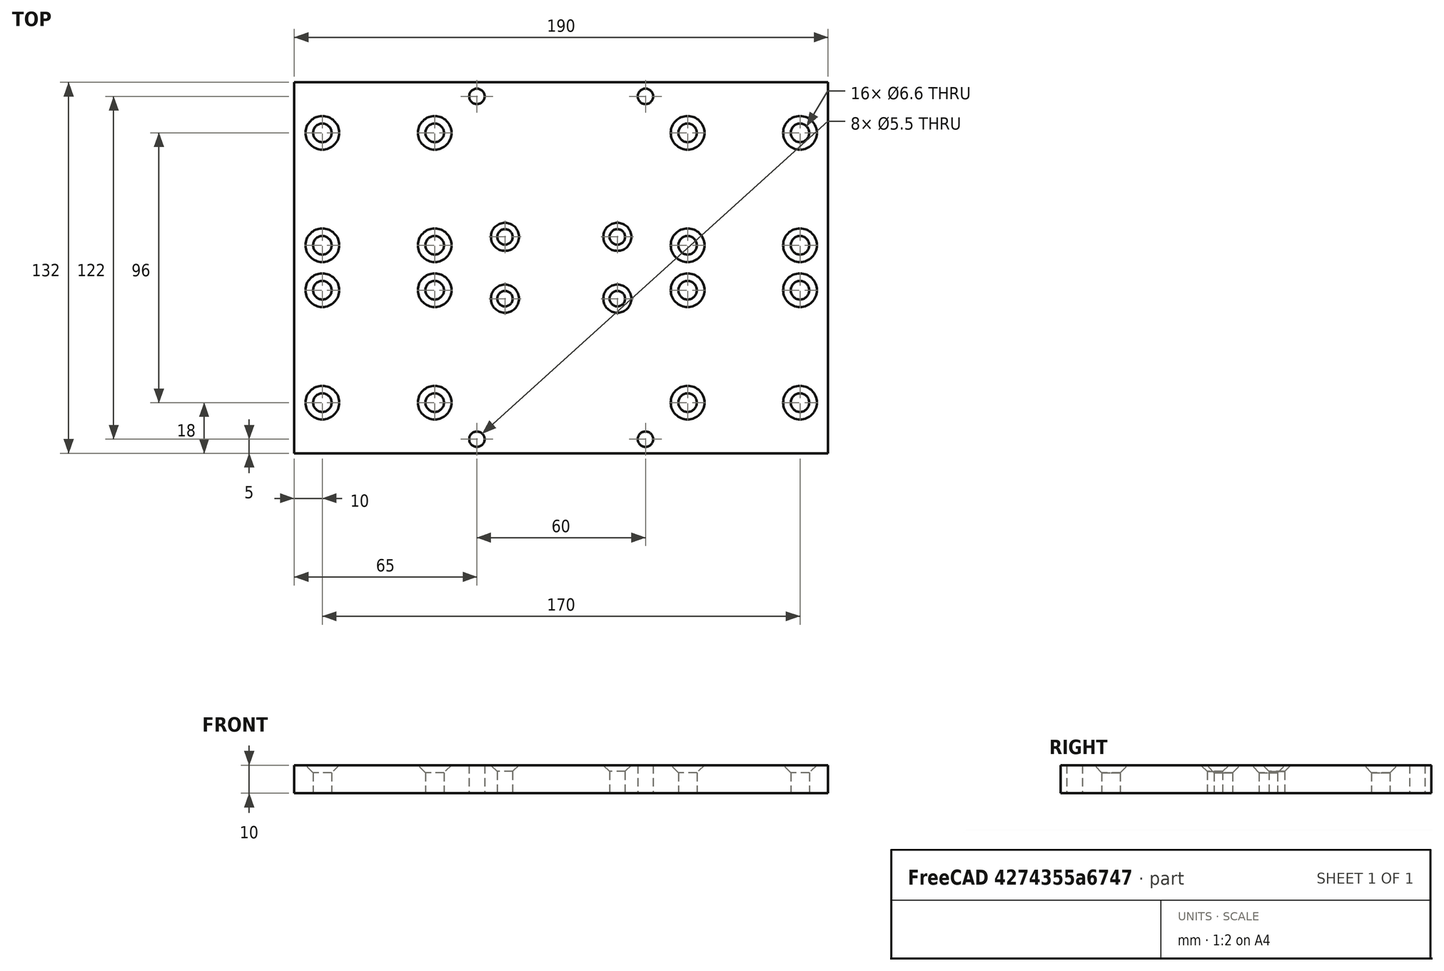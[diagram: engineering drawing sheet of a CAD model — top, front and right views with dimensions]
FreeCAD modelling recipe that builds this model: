
FCSTD DOCUMENT  (FreeCAD 0.17R13528 (Git))
Label: plate6
License: All rights reserved
LicenseURL: http://en.wikipedia.org/wiki/All_rights_reserved
objects: TechDraw::DrawViewDimension×83, PartDesign::LinearPattern×16, Sketcher::SketchObject×9, PartDesign::Hole×8, PartDesign::Body×2, TechDraw::DrawProjGroupItem×2, PartDesign::Pad×1, TechDraw::DrawSVGTemplate×1, TechDraw::DrawProjGroup×1, TechDraw::DrawPage×1
note: 45 computed .brp shape members not serialized (recipe doc carries the construction recipe); baked Part::Feature solids carry a one-line shape summary decoded from their .brp

FEATURE [PartDesign::Body] Body
  Origin = -> Origin
FEATURE [Sketcher::SketchObject] Sketch
  MapMode = 5
  Support = -> [XY_Plane001]
  sketch-geometry (4):
    g0: LineSegment StartX=0 StartY=0 StartZ=0 EndX=190 EndY=0 EndZ=0
    g1: LineSegment StartX=190 StartY=0 StartZ=0 EndX=190 EndY=132 EndZ=0
    g2: LineSegment StartX=190 StartY=132 StartZ=0 EndX=0 EndY=132 EndZ=0
    g3: LineSegment StartX=0 StartY=132 StartZ=0 EndX=0 EndY=0 EndZ=0
  constraints (11):
    c: Coincident(g0,g1)
    c: Coincident(g1,g2)
    c: Coincident(g2,g3)
    c: Coincident(g3,g0)
    c: Horizontal(g0)
    c: Horizontal(g2)
    c: Vertical(g1)
    c: Vertical(g3)
    c: Coincident(g0,g-1)
    c: DistanceX(g0,g0) = 190
    c: DistanceY(g3,g3) = 132
FEATURE [PartDesign::Pad] Pad
  Length = 10
  Length2 = 100
  Profile = -> Sketch
  Type = 0
FEATURE [Sketcher::SketchObject] Sketch001
  MapMode = 5
  Placement = pos=(0,0,10) rot=(0,0,1;0rad)
  Support = -> [Pad]
  sketch-geometry (1):
    g0: Circle CenterX=65 CenterY=5 CenterZ=0 NormalX=0 NormalY=0 NormalZ=1 AngleXU=0 Radius=4.6236
  constraints (2):
    c: Distance(g0,g-1) = 5
    c: Distance(g0,g-2) = 65
FEATURE [PartDesign::Hole] Hole
  BaseFeature = -> Pad
  Depth = 25
  DepthType = 1
  Diameter = 5.5
  DrillPoint = 0
  DrillPointAngle = 118
  HoleCutCountersinkAngle = 90
  HoleCutDepth = 0
  HoleCutDiameter = 5
  HoleCutType = 0
  ModelActualThread = false
  Profile = -> Sketch001
  Tapered = false
  TaperedAngle = 90
  ThreadAngle = 0
  ThreadClass = 0
  ThreadCutOffInner = 0
  ThreadCutOffOuter = 0
  ThreadDirection = 0
  ThreadFit = 0
  ThreadPitch = 0
  ThreadSize = 6
  ThreadType = 1
  Threaded = false
FEATURE [PartDesign::LinearPattern] LinearPattern
  BaseFeature = -> Hole
  Direction = -> Sketch001 [H_Axis]
  Length = 60
  Occurrences = 2
  Originals = -> [Hole]
FEATURE [PartDesign::LinearPattern] LinearPattern001
  BaseFeature = -> LinearPattern
  Direction = -> Sketch001 [V_Axis]
  Length = 122
  Occurrences = 2
  Originals = -> [Hole]
FEATURE [Sketcher::SketchObject] Sketch002
  MapMode = 5
  Placement = pos=(0,0,10) rot=(0,0,1;0rad)
  Support = -> [LinearPattern001]
  sketch-geometry (1):
    g0: Circle CenterX=10 CenterY=18 CenterZ=0 NormalX=0 NormalY=0 NormalZ=1 AngleXU=0 Radius=5.09329
  constraints (2):
    c: Distance(g0,g-2) = 10
    c: Distance(g0,g-1) = 18
FEATURE [PartDesign::Hole] Hole001
  BaseFeature = -> LinearPattern001
  Depth = 25
  DepthType = 1
  Diameter = 6.6
  DrillPoint = 0
  DrillPointAngle = 118
  HoleCutCountersinkAngle = 90
  HoleCutDepth = 0
  HoleCutDiameter = 12
  HoleCutType = 2
  ModelActualThread = false
  Profile = -> Sketch002
  Tapered = false
  TaperedAngle = 90
  ThreadAngle = 0
  ThreadClass = 0
  ThreadCutOffInner = 0
  ThreadCutOffOuter = 0
  ThreadDirection = 0
  ThreadFit = 0
  ThreadPitch = 0
  ThreadSize = 7
  ThreadType = 1
  Threaded = false
FEATURE [PartDesign::LinearPattern] LinearPattern002
  BaseFeature = -> Hole001
  Direction = -> Sketch002 [H_Axis]
  Length = 40
  Occurrences = 2
  Originals = -> [Hole001]
FEATURE [PartDesign::LinearPattern] LinearPattern003
  BaseFeature = -> LinearPattern002
  Direction = -> Sketch002 [H_Axis]
  Length = 170
  Occurrences = 2
  Originals = -> [Hole001]
FEATURE [PartDesign::LinearPattern] LinearPattern004
  BaseFeature = -> LinearPattern003
  Direction = -> Sketch002 [H_Axis]
  Length = 130
  Occurrences = 2
  Originals = -> [Hole001]
FEATURE [Sketcher::SketchObject] Sketch003
  MapMode = 5
  Placement = pos=(0,0,10) rot=(0,0,1;0rad)
  Support = -> [LinearPattern004]
  sketch-geometry (1):
    g0: Circle CenterX=10 CenterY=58 CenterZ=0 NormalX=0 NormalY=0 NormalZ=1 AngleXU=0 Radius=5.93075
  constraints (2):
    c: Distance(g0,g-2) = 10
    c: Distance(g0,g-1) = 58
FEATURE [PartDesign::Hole] Hole002
  BaseFeature = -> LinearPattern004
  Depth = 25
  DepthType = 1
  Diameter = 6.6
  DrillPoint = 0
  DrillPointAngle = 118
  HoleCutCountersinkAngle = 90
  HoleCutDepth = 0
  HoleCutDiameter = 12
  HoleCutType = 2
  ModelActualThread = false
  Profile = -> Sketch003
  Tapered = false
  TaperedAngle = 90
  ThreadAngle = 0
  ThreadClass = 0
  ThreadCutOffInner = 0
  ThreadCutOffOuter = 0
  ThreadDirection = 0
  ThreadFit = 0
  ThreadPitch = 0
  ThreadSize = 7
  ThreadType = 1
  Threaded = false
FEATURE [PartDesign::LinearPattern] LinearPattern005
  BaseFeature = -> Hole002
  Direction = -> Sketch003 [H_Axis]
  Length = 40
  Occurrences = 2
  Originals = -> [Hole002]
FEATURE [PartDesign::LinearPattern] LinearPattern006
  BaseFeature = -> LinearPattern005
  Direction = -> Sketch003 [H_Axis]
  Length = 130
  Occurrences = 2
  Originals = -> [Hole002]
FEATURE [PartDesign::LinearPattern] LinearPattern007
  BaseFeature = -> LinearPattern006
  Direction = -> Sketch003 [H_Axis]
  Length = 170
  Occurrences = 2
  Originals = -> [Hole002]
FEATURE [Sketcher::SketchObject] Sketch004
  MapMode = 5
  Placement = pos=(0,0,10) rot=(0,0,1;0rad)
  Support = -> [LinearPattern007]
  sketch-geometry (1):
    g0: Circle CenterX=10 CenterY=114 CenterZ=0 NormalX=0 NormalY=0 NormalZ=1 AngleXU=0 Radius=5.45983
  constraints (2):
    c: Distance(g0,g-1) = 114
    c: Distance(g0,g-2) = 10
FEATURE [PartDesign::Hole] Hole003
  BaseFeature = -> LinearPattern007
  Depth = 25
  DepthType = 1
  Diameter = 6.6
  DrillPoint = 0
  DrillPointAngle = 118
  HoleCutCountersinkAngle = 90
  HoleCutDepth = 0
  HoleCutDiameter = 12
  HoleCutType = 2
  ModelActualThread = false
  Profile = -> Sketch004
  Tapered = false
  TaperedAngle = 90
  ThreadAngle = 0
  ThreadClass = 0
  ThreadCutOffInner = 0
  ThreadCutOffOuter = 0
  ThreadDirection = 0
  ThreadFit = 0
  ThreadPitch = 0
  ThreadSize = 7
  ThreadType = 1
  Threaded = false
FEATURE [PartDesign::LinearPattern] LinearPattern008
  BaseFeature = -> Hole003
  Direction = -> Sketch004 [H_Axis]
  Length = 40
  Occurrences = 2
  Originals = -> [Hole003]
FEATURE [PartDesign::LinearPattern] LinearPattern009
  BaseFeature = -> LinearPattern008
  Direction = -> Sketch004 [H_Axis]
  Length = 130
  Occurrences = 2
  Originals = -> [Hole003]
FEATURE [PartDesign::LinearPattern] LinearPattern010
  BaseFeature = -> LinearPattern009
  Direction = -> Sketch004 [H_Axis]
  Length = 170
  Occurrences = 2
  Originals = -> [Hole003]
FEATURE [Sketcher::SketchObject] Sketch005
  MapMode = 5
  Placement = pos=(0,0,10) rot=(0,0,1;0rad)
  Support = -> [LinearPattern010]
  sketch-geometry (1):
    g0: Circle CenterX=125 CenterY=127 CenterZ=0 NormalX=0 NormalY=0 NormalZ=1 AngleXU=0 Radius=5.34356
  constraints (2):
    c: Distance(g0,g-1) = 127
    c: Distance(g0,g-2) = 125
FEATURE [PartDesign::Hole] Hole004
  BaseFeature = -> LinearPattern010
  Depth = 25
  DepthType = 1
  Diameter = 5.5
  DrillPoint = 0
  DrillPointAngle = 118
  HoleCutCountersinkAngle = 90
  HoleCutDepth = 0
  HoleCutDiameter = 5
  HoleCutType = 0
  ModelActualThread = false
  Profile = -> Sketch005
  Tapered = false
  TaperedAngle = 90
  ThreadAngle = 0
  ThreadClass = 0
  ThreadCutOffInner = 0
  ThreadCutOffOuter = 0
  ThreadDirection = 0
  ThreadFit = 0
  ThreadPitch = 0
  ThreadSize = 6
  ThreadType = 1
  Threaded = false
FEATURE [Sketcher::SketchObject] Sketch006
  MapMode = 5
  Placement = pos=(0,0,10) rot=(0,0,1;0rad)
  Support = -> [Hole004]
  sketch-geometry (1):
    g0: Circle CenterX=10 CenterY=74 CenterZ=0 NormalX=0 NormalY=0 NormalZ=1 AngleXU=0 Radius=5.11164
  constraints (2):
    c: Distance(g0,g-2) = 10
    c: Distance(g0,g-1) = 74
FEATURE [PartDesign::Hole] Hole005
  BaseFeature = -> Hole004
  Depth = 25
  DepthType = 1
  Diameter = 6.6
  DrillPoint = 0
  DrillPointAngle = 118
  HoleCutCountersinkAngle = 90
  HoleCutDepth = 0
  HoleCutDiameter = 12
  HoleCutType = 2
  ModelActualThread = false
  Profile = -> Sketch006
  Tapered = false
  TaperedAngle = 90
  ThreadAngle = 0
  ThreadClass = 0
  ThreadCutOffInner = 0
  ThreadCutOffOuter = 0
  ThreadDirection = 0
  ThreadFit = 0
  ThreadPitch = 0
  ThreadSize = 7
  ThreadType = 1
  Threaded = false
FEATURE [PartDesign::LinearPattern] LinearPattern011
  BaseFeature = -> Hole005
  Direction = -> Sketch006 [H_Axis]
  Length = 40
  Occurrences = 2
  Originals = -> [Hole005]
FEATURE [PartDesign::LinearPattern] LinearPattern012
  BaseFeature = -> LinearPattern011
  Direction = -> Sketch006 [H_Axis]
  Length = 130
  Occurrences = 2
  Originals = -> [Hole005]
FEATURE [PartDesign::LinearPattern] LinearPattern013
  BaseFeature = -> LinearPattern012
  Direction = -> Sketch006 [H_Axis]
  Length = 170
  Occurrences = 2
  Originals = -> [Hole005]
FEATURE [Sketcher::SketchObject] Sketch007
  MapMode = 5
  Placement = pos=(0,0,10) rot=(0,0,1;0rad)
  Support = -> [LinearPattern013]
  sketch-geometry (1):
    g0: Circle CenterX=75 CenterY=55 CenterZ=0 NormalX=0 NormalY=0 NormalZ=1 AngleXU=0 Radius=3.75047
  constraints (2):
    c: Distance(g0,g-1) = 55
    c: Distance(g0,g-2) = 75
FEATURE [PartDesign::Hole] Hole006
  BaseFeature = -> LinearPattern013
  Depth = 25
  DepthType = 1
  Diameter = 5.5
  DrillPoint = 0
  DrillPointAngle = 118
  HoleCutCountersinkAngle = 90
  HoleCutDepth = 0
  HoleCutDiameter = 10
  HoleCutType = 2
  ModelActualThread = false
  Profile = -> Sketch007
  Tapered = false
  TaperedAngle = 90
  ThreadAngle = 0
  ThreadClass = 0
  ThreadCutOffInner = 0
  ThreadCutOffOuter = 0
  ThreadDirection = 0
  ThreadFit = 0
  ThreadPitch = 0
  ThreadSize = 6
  ThreadType = 1
  Threaded = false
FEATURE [PartDesign::LinearPattern] LinearPattern014
  BaseFeature = -> Hole006
  Direction = -> Sketch007 [H_Axis]
  Length = 40
  Occurrences = 2
  Originals = -> [Hole006]
FEATURE [PartDesign::LinearPattern] LinearPattern015
  BaseFeature = -> LinearPattern014
  Direction = -> Sketch007 [V_Axis]
  Length = 22
  Occurrences = 2
  Originals = -> [Hole006]
FEATURE [Sketcher::SketchObject] Sketch008
  MapMode = 5
  Placement = pos=(0,0,10) rot=(0,0,1;0rad)
  Support = -> [LinearPattern015]
  sketch-geometry (1):
    g0: Circle CenterX=115 CenterY=77 CenterZ=0 NormalX=0 NormalY=0 NormalZ=1 AngleXU=0 Radius=5.25608
  constraints (2):
    c: Distance(g0,g-1) = 77
    c: Distance(g0,g-2) = 115
FEATURE [PartDesign::Hole] Hole007
  BaseFeature = -> LinearPattern015
  Depth = 25
  DepthType = 1
  Diameter = 5.5
  DrillPoint = 0
  DrillPointAngle = 118
  HoleCutCountersinkAngle = 90
  HoleCutDepth = 0
  HoleCutDiameter = 10
  HoleCutType = 2
  ModelActualThread = false
  Profile = -> Sketch008
  Tapered = false
  TaperedAngle = 90
  ThreadAngle = 0
  ThreadClass = 0
  ThreadCutOffInner = 0
  ThreadCutOffOuter = 0
  ThreadDirection = 0
  ThreadFit = 0
  ThreadPitch = 0
  ThreadSize = 6
  ThreadType = 1
  Threaded = false
FEATURE [PartDesign::Body] Body001
  Group = -> [Sketch,Pad,Sketch001,Hole,LinearPattern,LinearPattern001,Sketch002,Hole001,LinearPattern002,LinearPattern003,LinearPattern004,Sketch003,Hole002,LinearPattern005,LinearPattern006,LinearPattern007,Sketch004,Hole003,LinearPattern008,LinearPattern009,LinearPattern010,Sketch005,Hole004,Sketch006,Hole005,LinearPattern011,LinearPattern012,LinearPattern013,Sketch007,Hole006,LinearPattern014,+3 more]
  Origin = -> Origin001
  Tip = -> Hole007
FEATURE [TechDraw::DrawSVGTemplate] Template
  EditableTexts = Designed_by_Name=Lukas Winter; FC-Date=27.08.2018; FC-SC=1:1; FC-SH=1/1; FC-Title=COSI Measure v1.0; Subtitle=Mechanical assembly - plate 6
  Height = 210
  Orientation = 1
  Width = 297
FEATURE [TechDraw::DrawProjGroupItem] ProjItem  label="Front"
  CoarseView = false
  Direction = (0,0,1)
  Focus = 100
  HardHidden = false
  IsoCount = 0
  IsoHidden = false
  IsoVisible = false
  LockPosition = false
  Perspective = false
  Rotation = 0
  RotationVector = (1,0,0)
  ScaleType = 0
  SeamHidden = false
  SeamVisible = false
  SmoothHidden = false
  SmoothVisible = false
  Source = -> [Body001]
  Type = 0
  X = 0
  Y = 114
FEATURE [TechDraw::DrawProjGroupItem] ProjItem001  label="Left"
  CoarseView = false
  Direction = (-1,0,0)
  Focus = 100
  HardHidden = false
  IsoCount = 0
  IsoHidden = false
  IsoVisible = false
  LockPosition = false
  Perspective = false
  Rotation = 0
  RotationVector = (0,0,1)
  ScaleType = 0
  SeamHidden = false
  SeamVisible = false
  SmoothHidden = false
  SmoothVisible = false
  Source = -> [Body001]
  Type = 1
  X = 205
  Y = 0
FEATURE [TechDraw::DrawProjGroup] ProjGroup
  Anchor = -> ProjItem
  AutoDistribute = true
  CubeDirs = (6) [(0,-1,-6.12323e-17),(0,-6.12323e-17,1),(-1,0,0),(0,6.12323e-17,-1),(1,0,0),(0,1,6.12323e-17)]
  CubeRotations = (6) [(1,0,0),(1,0,0),(0,6.12323e-17,1),(-1,0,0),(0,-6.12323e-17,-1),(1,0,0)]
  LockPosition = false
  ProjectionType = 0
  Rotation = 0
  ScaleType = 0
  Source = -> [Body001]
  Views = -> [ProjItem,ProjItem001]
  X = 107.632
  Y = 124.591
  spacingX = 15
  spacingY = 15
FEATURE [TechDraw::DrawViewDimension] Dimension
  FormatSpec = %.2f
  LockPosition = false
  MeasureType = 1
  References2D = -> [ProjItem001]
  Rotation = 0
  ScaleType = 0
  Type = 1
  X = 18.3556
  Y = -56.6222
FEATURE [TechDraw::DrawViewDimension] Dimension001
  FormatSpec = %.2f
  LockPosition = false
  MeasureType = 1
  References2D = -> [ProjItem]
  Rotation = 0
  ScaleType = 0
  Type = 1
  X = 1.86667
  Y = 73.4222
FEATURE [TechDraw::DrawViewDimension] Dimension002
  FormatSpec = %.2f
  LockPosition = false
  MeasureType = 1
  References2D = -> [ProjItem001]
  Rotation = 0
  ScaleType = 0
  Type = 2
  X = 16.1778
  Y = -0.311111
FEATURE [TechDraw::DrawViewDimension] Dimension003 .. Dimension006  x4 (patterned run collapsed; names and placements below)
  FormatSpec = %.2f
  LockPosition = false
  MeasureType = 1
  Rotation = 0
  ScaleType = 0
  Type = 5
  X = 0
  Y = 0
FEATURE [TechDraw::DrawViewDimension] Dimension007
  FormatSpec = %.2f
  LockPosition = false
  MeasureType = 1
  Rotation = 0
  ScaleType = 0
  Type = 5
  X = 0.311111
  Y = 48.5333
FEATURE [TechDraw::DrawViewDimension] Dimension008
  FormatSpec = %.2f
  LockPosition = false
  MeasureType = 1
  Rotation = 0
  ScaleType = 0
  Type = 5
  X = 0.311111
  Y = 48.5333
FEATURE [TechDraw::DrawViewDimension] Dimension009
  FormatSpec = %.2f
  LockPosition = false
  MeasureType = 1
  Rotation = 0
  ScaleType = 0
  Type = 5
  X = 0.622222
  Y = -47.2889
FEATURE [TechDraw::DrawViewDimension] Dimension010
  FormatSpec = %.2f
  LockPosition = false
  MeasureType = 1
  Rotation = 0
  ScaleType = 0
  Type = 5
  X = 0.705063
  Y = -47.2889
FEATURE [TechDraw::DrawViewDimension] Dimension011
  FormatSpec = %.2f
  LockPosition = false
  MeasureType = 1
  Rotation = 0
  ScaleType = 0
  Type = 5
  X = -63.0489
  Y = 28.1164
FEATURE [TechDraw::DrawViewDimension] Dimension012
  FormatSpec = %.2f
  LockPosition = false
  MeasureType = 1
  Rotation = 0
  ScaleType = 0
  Type = 5
  X = -63.0042
  Y = 28.027
FEATURE [TechDraw::DrawViewDimension] Dimension013
  FormatSpec = %.2f
  LockPosition = false
  MeasureType = 1
  Rotation = 0
  ScaleType = 0
  Type = 5
  X = -63.1121
  Y = 28.1046
FEATURE [TechDraw::DrawViewDimension] Dimension016
  FormatSpec = %.2f
  LockPosition = false
  MeasureType = 1
  Rotation = 0
  ScaleType = 0
  Type = 5
  X = -66.0045
  Y = -28.2409
FEATURE [TechDraw::DrawViewDimension] Dimension017
  FormatSpec = %.2f
  LockPosition = false
  MeasureType = 1
  Rotation = 0
  ScaleType = 0
  Type = 5
  X = -65.9941
  Y = -28.1046
FEATURE [TechDraw::DrawViewDimension] Dimension019
  FormatSpec = %.2f
  LockPosition = false
  MeasureType = 1
  Rotation = 0
  ScaleType = 0
  Type = 5
  X = 68.207
  Y = 28.4333
FEATURE [TechDraw::DrawViewDimension] Dimension020
  FormatSpec = %.2f
  LockPosition = false
  MeasureType = 1
  Rotation = 0
  ScaleType = 0
  Type = 5
  X = 68.2455
  Y = 28.4727
FEATURE [TechDraw::DrawViewDimension] Dimension021
  FormatSpec = %.2f
  LockPosition = false
  MeasureType = 1
  Rotation = 0
  ScaleType = 0
  Type = 5
  X = 68.2221
  Y = 28.4196
FEATURE [TechDraw::DrawViewDimension] Dimension022
  FormatSpec = %.2f
  LockPosition = false
  MeasureType = 1
  Rotation = 0
  ScaleType = 0
  Type = 5
  X = 68.2448
  Y = 28.5482
FEATURE [TechDraw::DrawViewDimension] Dimension023
  FormatSpec = %.2f
  LockPosition = false
  MeasureType = 1
  Rotation = 0
  ScaleType = 0
  Type = 5
  X = 67.5154
  Y = -25.5658
FEATURE [TechDraw::DrawViewDimension] Dimension024
  FormatSpec = %.2f
  LockPosition = false
  MeasureType = 1
  Rotation = 0
  ScaleType = 0
  Type = 5
  X = 67.5629
  Y = -25.5486
FEATURE [TechDraw::DrawViewDimension] Dimension025
  FormatSpec = %.2f
  LockPosition = false
  MeasureType = 1
  Rotation = 0
  ScaleType = 0
  Type = 5
  X = 67.5664
  Y = -25.6646
FEATURE [TechDraw::DrawViewDimension] Dimension026
  FormatSpec = %.2f
  LockPosition = false
  MeasureType = 1
  Rotation = 0
  ScaleType = 0
  Type = 5
  X = 67.5189
  Y = -25.4605
FEATURE [TechDraw::DrawViewDimension] Dimension027
  FormatSpec = %.2f
  LockPosition = false
  MeasureType = 1
  Rotation = 0
  ScaleType = 0
  Type = 1
  X = -59.1111
  Y = -57.2963
FEATURE [TechDraw::DrawViewDimension] Dimension028
  FormatSpec = %.2f
  LockPosition = false
  MeasureType = 1
  Rotation = 0
  ScaleType = 0
  Type = 1
  X = 5.18518
  Y = -57.2963
FEATURE [TechDraw::DrawViewDimension] Dimension029
  FormatSpec = %.2f
  LockPosition = false
  MeasureType = 1
  Rotation = 0
  ScaleType = 0
  Type = 2
  X = 33.963
  Y = -49.5185
FEATURE [TechDraw::DrawViewDimension] Dimension030
  FormatSpec = %.2f
  LockPosition = false
  MeasureType = 1
  Rotation = 0
  ScaleType = 0
  Type = 1
  X = 65.5926
  Y = -44.0741
FEATURE [TechDraw::DrawViewDimension] Dimension031
  FormatSpec = %.2f
  LockPosition = false
  MeasureType = 1
  Rotation = 0
  ScaleType = 0
  Type = 1
  X = 70.7778
  Y = -55.4815
FEATURE [TechDraw::DrawViewDimension] Dimension032
  FormatSpec = %.2f
  LockPosition = false
  MeasureType = 1
  Rotation = 0
  ScaleType = 0
  Type = 2
  X = 99.8148
  Y = -37.8519
FEATURE [TechDraw::DrawViewDimension] Dimension033
  FormatSpec = %.2f
  LockPosition = false
  MeasureType = 1
  Rotation = 0
  ScaleType = 0
  Type = 2
  X = 88.9259
  Y = -29.037
FEATURE [TechDraw::DrawViewDimension] Dimension034
  FormatSpec = %.2f
  LockPosition = false
  MeasureType = 1
  Rotation = 0
  ScaleType = 0
  Type = 2
  X = -75.9773
  Y = -78.8567
FEATURE [TechDraw::DrawViewDimension] Dimension035
  FormatSpec = %.2f
  LockPosition = false
  MeasureType = 1
  Rotation = 0
  ScaleType = 0
  Type = 1
  X = -85.7591
  Y = -54.0792
FEATURE [TechDraw::DrawViewDimension] Dimension036
  FormatSpec = %.2f
  LockPosition = false
  MeasureType = 1
  Rotation = 0
  ScaleType = 0
  Type = 2
  X = -92.2963
  Y = -29.5556
FEATURE [TechDraw::DrawViewDimension] Dimension038
  FormatSpec = %.2f
  LockPosition = false
  MeasureType = 1
  Rotation = 0
  ScaleType = 0
  Type = 2
  X = -77.7778
  Y = 18.4074
FEATURE [TechDraw::DrawViewDimension] Dimension039
  FormatSpec = %.2f
  LockPosition = false
  MeasureType = 1
  Rotation = 0
  ScaleType = 0
  Type = 2
  X = -60.4074
  Y = 1.55556
FEATURE [TechDraw::DrawViewDimension] Dimension040
  FormatSpec = %.2f
  LockPosition = false
  MeasureType = 1
  Rotation = 0
  ScaleType = 0
  Type = 1
  X = -65.3333
  Y = 58.8518
FEATURE [TechDraw::DrawViewDimension] Dimension041
  FormatSpec = %.2f
  LockPosition = false
  MeasureType = 1
  Rotation = 0
  ScaleType = 0
  Type = 2
  X = -32.1481
  Y = -0.518519
FEATURE [TechDraw::DrawViewDimension] Dimension042
  FormatSpec = %.2f
  LockPosition = false
  MeasureType = 1
  Rotation = 0
  ScaleType = 0
  Type = 1
  X = 0.518519
  Y = -16.3333
FEATURE [TechDraw::DrawViewDimension] Dimension043
  FormatSpec = %.2f
  LockPosition = false
  MeasureType = 1
  Rotation = 0
  ScaleType = 0
  Type = 2
  X = -23.3333
  Y = -38.8889
FEATURE [TechDraw::DrawViewDimension] Dimension044
  FormatSpec = %.2f
  LockPosition = false
  MeasureType = 1
  Rotation = 0
  ScaleType = 0
  Type = 1
  X = 3.11111
  Y = 64.8148
FEATURE [TechDraw::DrawViewDimension] Dimension045
  FormatSpec = %.2f
  LockPosition = false
  MeasureType = 1
  Rotation = 0
  ScaleType = 0
  Type = 1
  X = -49.2593
  Y = 64.8148
FEATURE [TechDraw::DrawViewDimension] Dimension046
  FormatSpec = %.2f
  LockPosition = false
  MeasureType = 1
  Rotation = 0
  ScaleType = 0
  Type = 2
  X = 34.7407
  Y = 58.5926
FEATURE [TechDraw::DrawViewDimension] Dimension047
  FormatSpec = %.2f
  LockPosition = false
  MeasureType = 1
  Rotation = 0
  ScaleType = 0
  Type = 2
  X = 78.2963
  Y = 22.2963
FEATURE [TechDraw::DrawViewDimension] Dimension048
  FormatSpec = %.2f
  LockPosition = false
  MeasureType = 1
  Rotation = 0
  ScaleType = 0
  Type = 2
  X = 51.5926
  Y = 0.259259
FEATURE [TechDraw::DrawViewDimension] Dimension049
  FormatSpec = %.2f
  LockPosition = false
  MeasureType = 1
  Rotation = 0
  ScaleType = 0
  Type = 1
  X = -55.8343
  Y = 22.8449
FEATURE [TechDraw::DrawViewDimension] Dimension050
  FormatSpec = %.2f
  LockPosition = false
  MeasureType = 1
  Rotation = 0
  ScaleType = 0
  Type = 2
  X = 100.987
  Y = 56.443
FEATURE [TechDraw::DrawViewDimension] Dimension051
  FormatSpec = %.2f
  LockPosition = false
  MeasureType = 1
  Rotation = 0
  ScaleType = 0
  Type = 1
  X = 74.4438
  Y = 64.6807
FEATURE [TechDraw::DrawViewDimension] Dimension054
  FormatSpec = %.2f
  LockPosition = false
  MeasureType = 1
  References2D = -> [ProjItem]
  Rotation = 0
  ScaleType = 0
  Type = 1
  X = 0
  Y = -7.23844
FEATURE [TechDraw::DrawViewDimension] Dimension055
  FormatSpec = %.2f
  LockPosition = false
  MeasureType = 1
  References2D = -> [ProjItem]
  Rotation = 0
  ScaleType = 0
  Type = 2
  X = -24.1281
  Y = 5.12723
FEATURE [TechDraw::DrawViewDimension] Dimension056
  FormatSpec = %.2f
  LockPosition = false
  MeasureType = 1
  References2D = -> [ProjItem]
  Rotation = 0
  ScaleType = 0
  Type = 2
  X = -23.8265
  Y = -42.8274
FEATURE [TechDraw::DrawViewDimension] Dimension057
  FormatSpec = %.2f
  LockPosition = false
  MeasureType = 1
  References2D = -> [ProjItem]
  Rotation = 0
  ScaleType = 0
  Type = 1
  X = 3.92082
  Y = -57.3043
FEATURE [TechDraw::DrawViewDimension] Dimension058
  FormatSpec = %.2f
  LockPosition = false
  MeasureType = 1
  References2D = -> [ProjItem]
  Rotation = 0
  ScaleType = 0
  Type = 0
  X = -58.8123
  Y = -57.0027
FEATURE [TechDraw::DrawViewDimension] Dimension059
  FormatSpec = %.2f
  LockPosition = false
  MeasureType = 1
  References2D = -> [ProjItem]
  Rotation = 0
  ScaleType = 0
  Type = 2
  X = 32.8746
  Y = -50.0658
FEATURE [TechDraw::DrawViewDimension] Dimension060
  FormatSpec = %.2f
  LockPosition = false
  MeasureType = 1
  References2D = -> [ProjItem]
  Rotation = 0
  ScaleType = 0
  Type = 1
  X = 65.1459
  Y = -44.3354
FEATURE [TechDraw::DrawViewDimension] Dimension061
  FormatSpec = %.2f
  LockPosition = false
  MeasureType = 1
  References2D = -> [ProjItem]
  Rotation = 0
  ScaleType = 0
  Type = 1
  X = 88.9724
  Y = -57.3043
FEATURE [TechDraw::DrawViewDimension] Dimension062
  FormatSpec = %.2f
  LockPosition = false
  MeasureType = 1
  References2D = -> [ProjItem]
  Rotation = 0
  ScaleType = 0
  Type = 2
  X = 51.2723
  Y = -56.0979
FEATURE [TechDraw::DrawViewDimension] Dimension063
  FormatSpec = %.2f
  LockPosition = false
  MeasureType = 1
  References2D = -> [ProjItem]
  Rotation = 0
  ScaleType = 0
  Type = 2
  X = 81.4324
  Y = -26.8425
FEATURE [TechDraw::DrawViewDimension] Dimension064
  FormatSpec = %.2f
  LockPosition = false
  MeasureType = 1
  References2D = -> [ProjItem]
  Rotation = 0
  ScaleType = 0
  Type = 2
  X = 55.7963
  Y = 0.904805
FEATURE [TechDraw::DrawViewDimension] Dimension066
  FormatSpec = %.2f
  LockPosition = false
  MeasureType = 1
  References2D = -> [ProjItem]
  Rotation = 0
  ScaleType = 0
  Type = 1
  X = -55.7963
  Y = -18.6993
FEATURE [TechDraw::DrawViewDimension] Dimension067
  FormatSpec = %.2f
  LockPosition = false
  MeasureType = 1
  References2D = -> [ProjItem]
  Rotation = 0
  ScaleType = 0
  Type = 2
  X = -60.0187
  Y = 1.20641
FEATURE [TechDraw::DrawViewDimension] Dimension068
  FormatSpec = %.2f
  LockPosition = false
  MeasureType = 1
  References2D = -> [ProjItem]
  Rotation = 0
  ScaleType = 0
  Type = 1
  X = -86.258
  Y = -33.4778
FEATURE [TechDraw::DrawViewDimension] Dimension069
  FormatSpec = %.2f
  LockPosition = false
  MeasureType = 1
  References2D = -> [ProjItem]
  Rotation = 0
  ScaleType = 0
  Type = 2
  X = -76.6068
  Y = -56.7011
FEATURE [TechDraw::DrawViewDimension] Dimension070
  FormatSpec = %.2f
  LockPosition = false
  MeasureType = 1
  References2D = -> [ProjItem]
  Rotation = 0
  ScaleType = 0
  Type = 1
  X = -60.0187
  Y = -40.4146
FEATURE [TechDraw::DrawViewDimension] Dimension071
  FormatSpec = %.2f
  LockPosition = false
  MeasureType = 1
  References2D = -> [ProjItem]
  Rotation = 0
  ScaleType = 0
  Type = 2
  X = -35.8906
  Y = -34.6842
FEATURE [TechDraw::DrawViewDimension] Dimension072
  FormatSpec = %.2f
  LockPosition = false
  MeasureType = 1
  References2D = -> [ProjItem]
  Rotation = 0
  ScaleType = 0
  Type = 2
  X = 81.4324
  Y = 29.5569
FEATURE [TechDraw::DrawViewDimension] Dimension073
  FormatSpec = %.2f
  LockPosition = false
  MeasureType = 1
  References2D = -> [ProjItem]
  Rotation = 0
  ScaleType = 0
  Type = 2
  X = 81.4324
  Y = 63.3363
FEATURE [TechDraw::DrawViewDimension] Dimension074
  FormatSpec = %.2f
  LockPosition = false
  MeasureType = 1
  References2D = -> [ProjItem]
  Rotation = 0
  ScaleType = 0
  Type = 1
  X = 104.957
  Y = 43.129
FEATURE [TechDraw::DrawViewDimension] Dimension075
  FormatSpec = %.2f
  LockPosition = false
  MeasureType = 1
  References2D = -> [ProjItem]
  Rotation = 0
  ScaleType = 0
  Type = 1
  X = -65.4475
  Y = 64.5427
FEATURE [TechDraw::DrawViewDimension] Dimension076
  FormatSpec = %.2f
  LockPosition = false
  MeasureType = 1
  References2D = -> [ProjItem]
  Rotation = 0
  ScaleType = 0
  Type = 1
  X = -0.301602
  Y = 64.5427
FEATURE [TechDraw::DrawViewDimension] Dimension077
  FormatSpec = %.2f
  LockPosition = false
  MeasureType = 1
  References2D = -> [ProjItem]
  Rotation = 0
  ScaleType = 0
  Type = 1
  X = 57.3043
  Y = 64.5427
FEATURE [TechDraw::DrawViewDimension] Dimension078
  FormatSpec = %.2f
  LockPosition = false
  MeasureType = 1
  References2D = -> [ProjItem]
  Rotation = 0
  ScaleType = 0
  Type = 2
  X = 20.5089
  Y = 50.9707
FEATURE [TechDraw::DrawViewDimension] Dimension079
  FormatSpec = %.2f
  LockPosition = false
  MeasureType = 1
  References2D = -> [ProjItem]
  Rotation = 0
  ScaleType = 0
  Type = 2
  X = -35.8906
  Y = 29.2553
FEATURE [TechDraw::DrawViewDimension] Dimension080
  FormatSpec = %.2f
  LockPosition = false
  MeasureType = 1
  References2D = -> [ProjItem]
  Rotation = 0
  ScaleType = 0
  Type = 1
  X = -65.1459
  Y = 51.5739
FEATURE [TechDraw::DrawViewDimension] Dimension081
  FormatSpec = %.2f
  LockPosition = false
  MeasureType = 1
  References2D = -> [ProjItem]
  Rotation = 0
  ScaleType = 0
  Type = 1
  X = 66.9555
  Y = 51.5739
FEATURE [TechDraw::DrawViewDimension] Dimension082
  FormatSpec = %.2f
  LockPosition = false
  MeasureType = 1
  References2D = -> [ProjItem]
  Rotation = 0
  ScaleType = 0
  Type = 5
  X = -10.8577
  Y = 29.8585
FEATURE [TechDraw::DrawViewDimension] Dimension083
  FormatSpec = %.2f
  LockPosition = false
  MeasureType = 1
  References2D = -> [ProjItem]
  Rotation = 0
  ScaleType = 0
  Type = 5
  X = -9.65125
  Y = 22.3185
FEATURE [TechDraw::DrawViewDimension] Dimension084
  FormatSpec = %.2f
  LockPosition = false
  MeasureType = 1
  References2D = -> [ProjItem]
  Rotation = 0
  ScaleType = 0
  Type = 5
  X = -55.4947
  Y = 27.7473
FEATURE [TechDraw::DrawViewDimension] Dimension085
  FormatSpec = %.2f
  LockPosition = false
  MeasureType = 1
  References2D = -> [ProjItem]
  Rotation = 0
  ScaleType = 0
  Type = 5
  X = -55.1931
  Y = 35.8906
FEATURE [TechDraw::DrawViewDimension] Dimension086
  FormatSpec = %.2f
  LockPosition = false
  MeasureType = 1
  References2D = -> [ProjItem]
  Rotation = 0
  ScaleType = 0
  Type = 5
  X = 0.904805
  Y = 51.2723
FEATURE [TechDraw::DrawViewDimension] Dimension087
  FormatSpec = %.2f
  LockPosition = false
  MeasureType = 1
  References2D = -> [ProjItem]
  Rotation = 0
  ScaleType = 0
  Type = 5
  X = 0.904805
  Y = 51.2723
FEATURE [TechDraw::DrawViewDimension] Dimension088
  FormatSpec = %.2f
  LockPosition = false
  MeasureType = 1
  References2D = -> [ProjItem]
  Rotation = 0
  ScaleType = 0
  Type = 5
  X = 10.2545
  Y = -46.7482
FEATURE [TechDraw::DrawViewDimension] Dimension089
  FormatSpec = %.2f
  LockPosition = false
  MeasureType = 1
  References2D = -> [ProjItem]
  Rotation = 0
  ScaleType = 0
  Type = 5
  X = 10.2545
  Y = -46.7482
FEATURE [TechDraw::DrawPage] Page
  KeepUpdated = true
  ProjectionType = 0
  Template = -> Template
  Views = -> [ProjGroup,Dimension,Dimension001,Dimension002,Dimension003,Dimension004,Dimension005,Dimension006,Dimension007,Dimension008,Dimension009,Dimension010,Dimension011,Dimension012,Dimension013,Dimension016,Dimension017,Dimension019,Dimension020,Dimension021,Dimension022,Dimension023,Dimension024,Dimension025,Dimension026,Dimension027,Dimension028,Dimension029,Dimension030,Dimension031,Dimension032,+53 more]
